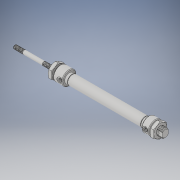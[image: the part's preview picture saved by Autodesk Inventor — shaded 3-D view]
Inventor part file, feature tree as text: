
AUTODESK INVENTOR PART (.ipt)
format: ipt  version: 2018 (Build 220112000, 112)  size: 1,830,400 bytes
history: native  units: in
note: dims shown in document units (in); Inventor stores cm internally (conversion verified against a paired STEP export)
features: other x3, revolve x1, boolean_combine x1
ambient origin geometry x8: Origin, YZ Plane, XZ Plane, XY Plane, X Axis, Y Axis, Z Axis, Center Point
bodies: Solid1 (feature_tree), Solid2 (feature_tree), Solid3 (feature_tree), Solid4 (feature_tree), Solid5 (feature_tree)
feature tree (5):
  other  "Cut-Extrude4"
  revolve  "Revolve4"  [1 undecoded]
  other  "Body-Move_Copy3"
  boolean_combine  "Combine3"
  other  "Cut-Extrude8"
note: 1 required parameter value undecoded (feature->parameter linkage not recoverable at this tier; creation-order binding heuristic only, values carry confidence <= 0.55)
